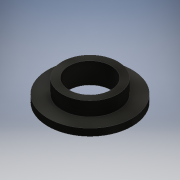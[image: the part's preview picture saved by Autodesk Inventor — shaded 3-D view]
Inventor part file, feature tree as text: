
AUTODESK INVENTOR PART (.ipt)
format: ipt  version: 2016 (Build 200138000, 138)  size: 108,544 bytes
history: native  units: mm
features: extrude x2, other x1, sketch x1
ambient origin geometry x8: Origin, YZ Plane, XZ Plane, XY Plane, X Axis, Y Axis, Z Axis, Center Point
bodies: Body1 (feature_tree)
feature tree (4):
  other  "ソリッド1"
  sketch  "スケッチ1"
  extrude  "押し出し1"  Depth=6.0mm
  extrude  "押し出し2"  Depth=8.0mm
